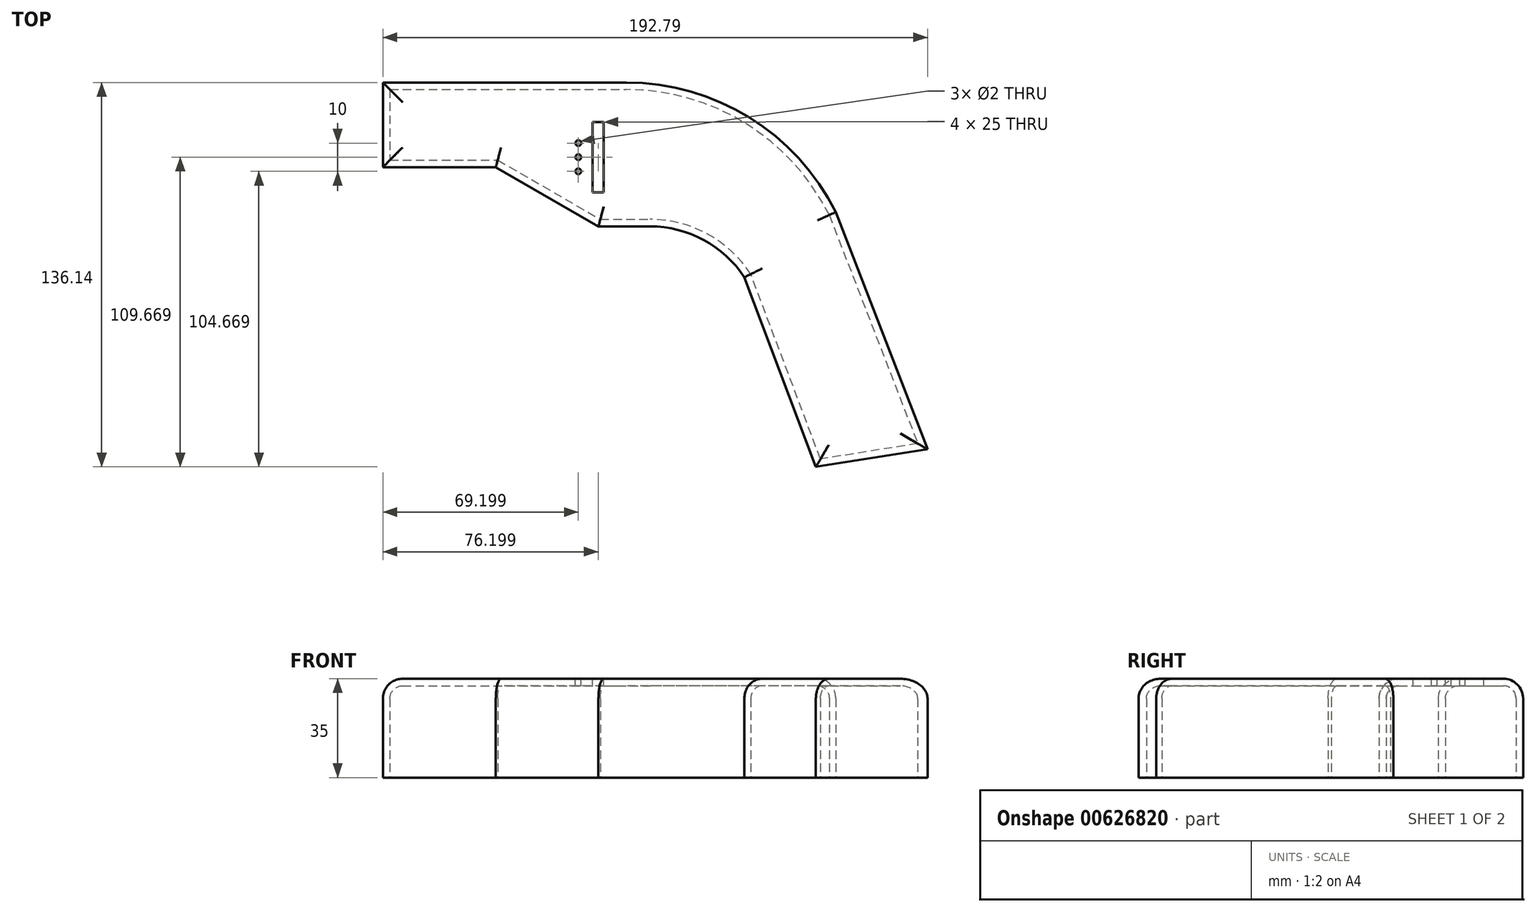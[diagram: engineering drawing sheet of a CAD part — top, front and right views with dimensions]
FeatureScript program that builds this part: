
annotation { "Feature Type Name" : "Feature", "Feature Type Description" : "" }
export const myFeature = defineFeature(function(context is Context, id is Id, definition is map)
    precondition{}
    {
        {
            var Q0;
            Q0=qCreatedBy(makeId("Top.planeOp"),FACE);
            var sketch = newSketch(context, id + "F0", { "sketchPlane" : qUnion([Q0])});
            skLineSegment(sketch, "E0", {"start": v(-115, 0) * mm, "end": v(-28.86, 0) * mm});
            skLineSegment(sketch, "E1", {"start": v(-115, 0) * mm, "end": v(-115, -30) * mm});
            skLineSegment(sketch, "E2", {"start": v(-115, -30) * mm, "end": v(-75, -30) * mm});
            skLineSegment(sketch, "E3", {"start": v(-75, -30) * mm, "end": v(-38.68, -50.97) * mm});
            skLineSegment(sketch, "E4", {"start": v(-38.68, -50.97) * mm, "end": v(-20.46, -50.97) * mm});
            skPoint(sketch, "E5", {"position": v(41.73, -37.75) * mm});
            skPoint(sketch, "E6.visualSharp", {"position": v(0, 0) * mm});
            skPoint(sketch, "E7.end.orphan", {"position": v(131.73, -119.16) * mm});
            skPoint(sketch, "E8.visualSharp", {"position": v(0, -50.97) * mm});
            skArc(sketch, "E9", {"start": v(12.98, -69.03) * mm, "mid": v(-1.46, -55.78) * mm, "end": v(-20.46, -50.97) * mm});
            skArc(sketch, "E10", {"start": v(45.3, -45.94) * mm, "mid": v(14.76, -12.42) * mm, "end": v(-28.86, 0) * mm});
            skLineSegment(sketch, "E11", {"start": v(45.3, -45.94) * mm, "end": v(77.8, -129.87) * mm});
            skLineSegment(sketch, "E12", {"start": v(77.8, -129.87) * mm, "end": v(38.28, -136.14) * mm});
            skLineSegment(sketch, "E13", {"start": v(38.28, -136.14) * mm, "end": v(12.98, -69.03) * mm});
            skSolve(sketch);
        }
        {
            var Q0;
            Q0 = qSketchRegion(id + "F0", true);
            extrude(context, id + "F1", {"entities" : qUnion([Q0]), "depth" : 35 * mm, "offsetDistance" : 25 * mm});
        }
        {
            var Q0;
            Q0=makeQuery(id+"F1.opExtrude","CAP_FACE",FACE,{"disambiguationData":[OSD([sQuery(id+"F0.wireOp",EDGE,"E0"),sQuery(id+"F0.wireOp",EDGE,"E1"),sQuery(id+"F0.wireOp",EDGE,"E2"),sQuery(id+"F0.wireOp",EDGE,"E3"),sQuery(id+"F0.wireOp",EDGE,"E4"),sQuery(id+"F0.wireOp",EDGE,"E9"),sQuery(id+"F0.wireOp",EDGE,"E10"),sQuery(id+"F0.wireOp",EDGE,"E11"),sQuery(id+"F0.wireOp",EDGE,"E12"),sQuery(id+"F0.wireOp",EDGE,"E13")])],"isStart":false});
            fillet(context, id + "F2", {"entities" : qUnion([Q0]), "radius" : 7 * mm, "tangentPropagation" : true, "allowEdgeOverflow" : false});
        }
        {
            var Q0;
            Q0=makeQuery(id+"F1.opExtrude","CAP_FACE",FACE,{"disambiguationData":[OSD([sQuery(id+"F0.wireOp",EDGE,"E0"),sQuery(id+"F0.wireOp",EDGE,"E1"),sQuery(id+"F0.wireOp",EDGE,"E2"),sQuery(id+"F0.wireOp",EDGE,"E3"),sQuery(id+"F0.wireOp",EDGE,"E4"),sQuery(id+"F0.wireOp",EDGE,"E9"),sQuery(id+"F0.wireOp",EDGE,"E10"),sQuery(id+"F0.wireOp",EDGE,"E11"),sQuery(id+"F0.wireOp",EDGE,"E12"),sQuery(id+"F0.wireOp",EDGE,"E13")])],"isStart":true});
            shell(context, id + "F3", {"entities" : qUnion([Q0]), "thickness" : 2.5 * mm});
        }
        {
            var Q0;
            Q0=makeQuery(id+"F1.opExtrude","CAP_FACE",FACE,{"disambiguationData":[OSD([sQuery(id+"F0.wireOp",EDGE,"E0"),sQuery(id+"F0.wireOp",EDGE,"E1"),sQuery(id+"F0.wireOp",EDGE,"E2"),sQuery(id+"F0.wireOp",EDGE,"E3"),sQuery(id+"F0.wireOp",EDGE,"E4"),sQuery(id+"F0.wireOp",EDGE,"E9"),sQuery(id+"F0.wireOp",EDGE,"E10"),sQuery(id+"F0.wireOp",EDGE,"E11"),sQuery(id+"F0.wireOp",EDGE,"E12"),sQuery(id+"F0.wireOp",EDGE,"E13")])],"isStart":false});
            var sketch = newSketch(context, id + "F4", { "sketchPlane" : qUnion([Q0])});
            skLineSegment(sketch, "E14.bottom", {"start": v(-36.8, -38.97) * mm, "end": v(-40.8, -38.97) * mm});
            skLineSegment(sketch, "E14.top", {"start": v(-36.8, -13.97) * mm, "end": v(-40.8, -13.97) * mm});
            skLineSegment(sketch, "E14.left", {"start": v(-36.8, -38.97) * mm, "end": v(-36.8, -13.97) * mm});
            skLineSegment(sketch, "E14.right", {"start": v(-40.8, -38.97) * mm, "end": v(-40.8, -13.97) * mm});
            skLineSegment(sketch, "E15", {"start": v(-36.8, -38.97) * mm, "end": v(-36.8, -31.47) * mm});
            skLineSegment(sketch, "E16", {"start": v(-36.8, -13.97) * mm, "end": v(-36.8, -21.47) * mm});
            skLineSegment(sketch, "E17", {"start": v(-36.8, -21.47) * mm, "end": v(-36.8, -26.47) * mm});
            skCircle(sketch, "E18", {"center": v(-45.8, -21.47) * mm, "radius": 1 * mm});
            skCircle(sketch, "E19", {"center": v(-45.8, -26.47) * mm, "radius": 1 * mm});
            skPoint(sketch, "E19.centerSnap0", {"position": v(-40.8, -26.47) * mm});
            skCircle(sketch, "E20", {"center": v(-45.8, -31.47) * mm, "radius": 1 * mm});
            skSolve(sketch);
        }
        {
            var Q0;
            Q0 = qSketchRegion(id + "F4", true);
            extrude(context, id + "F5", {"entities" : qUnion([Q0]), "operationType" : NewBodyOperationType.REMOVE, "endBound" : BoundingType.THROUGH_ALL, "oppositeDirection" : true, "depth" : 25 * mm, "offsetDistance" : 25 * mm});
        }
    });
